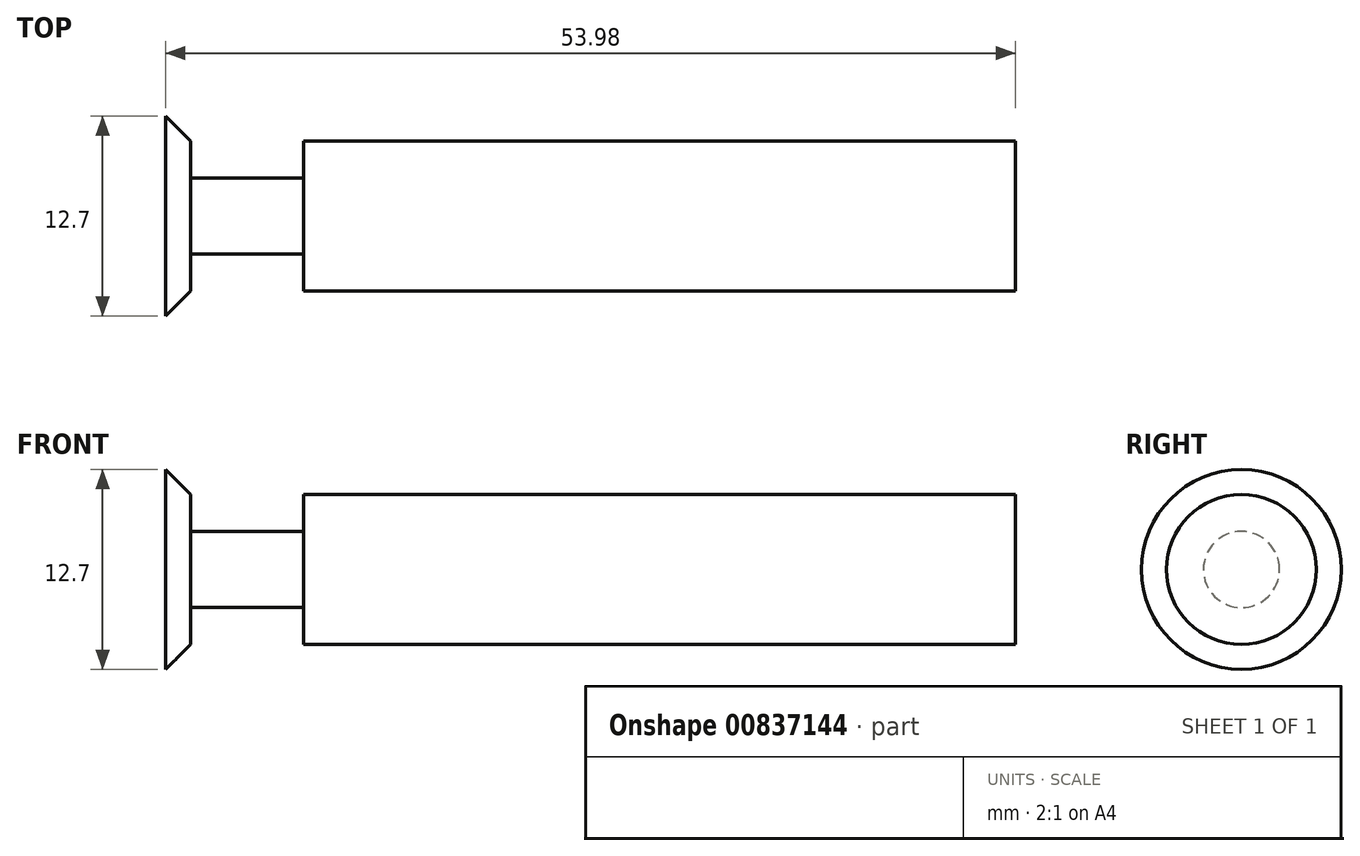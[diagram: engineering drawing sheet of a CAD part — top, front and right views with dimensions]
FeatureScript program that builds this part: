
annotation { "Feature Type Name" : "Feature", "Feature Type Description" : "" }
export const myFeature = defineFeature(function(context is Context, id is Id, definition is map)
    precondition{}
    {
        {
            var Q0;
            Q0=qCreatedBy(makeId("Top.planeOp"),FACE);
            var sketch = newSketch(context, id + "F0", { "sketchPlane" : qUnion([Q0])});
            skLineSegment(sketch, "E0", {"start": v(0, 0) * mm, "end": v(0, 6.35) * mm});
            skLineSegment(sketch, "E1", {"start": v(0, 6.35) * mm, "end": v(1.59, 4.76) * mm});
            skLineSegment(sketch, "E2", {"start": v(53.98, 4.76) * mm, "end": v(53.98, 0) * mm});
            skLineSegment(sketch, "E3", {"start": v(53.97, 0) * mm, "end": v(0, 0) * mm});
            skLineSegment(sketch, "E4", {"start": v(0, 0) * mm, "end": v(-5.72, 0) * mm, "construction": true});
            skLineSegment(sketch, "E5", {"start": v(8.76, 2.41) * mm, "end": v(8.76, 2.41) * mm});
            skLineSegment(sketch, "E6", {"start": v(8.76, 2.41) * mm, "end": v(3.94, 2.41) * mm});
            skLineSegment(sketch, "E7", {"start": v(8.76, 2.41) * mm, "end": v(8.76, 4.76) * mm});
            skLineSegment(sketch, "E8", {"start": v(8.76, 4.76) * mm, "end": v(53.98, 4.76) * mm});
            skLineSegment(sketch, "E9", {"start": v(1.59, 4.76) * mm, "end": v(1.59, 2.41) * mm});
            skLineSegment(sketch, "E10", {"start": v(1.59, 2.41) * mm, "end": v(3.94, 2.41) * mm});
            skSolve(sketch);
        }
        {
            var Q0;
            Q0 = qSketchRegion(id + "F0", true);
            var Q1;
            Q1=sQuery(id+"F0.wireOp",EDGE,"E4");
            revolve(context, id + "F1", {"surfaceOperationType" : NewSurfaceOperationType.NEW, "entities" : qUnion([Q0]), "axis" : qUnion([Q1]), "revolveType" : RevolveType.FULL});
        }
    });
